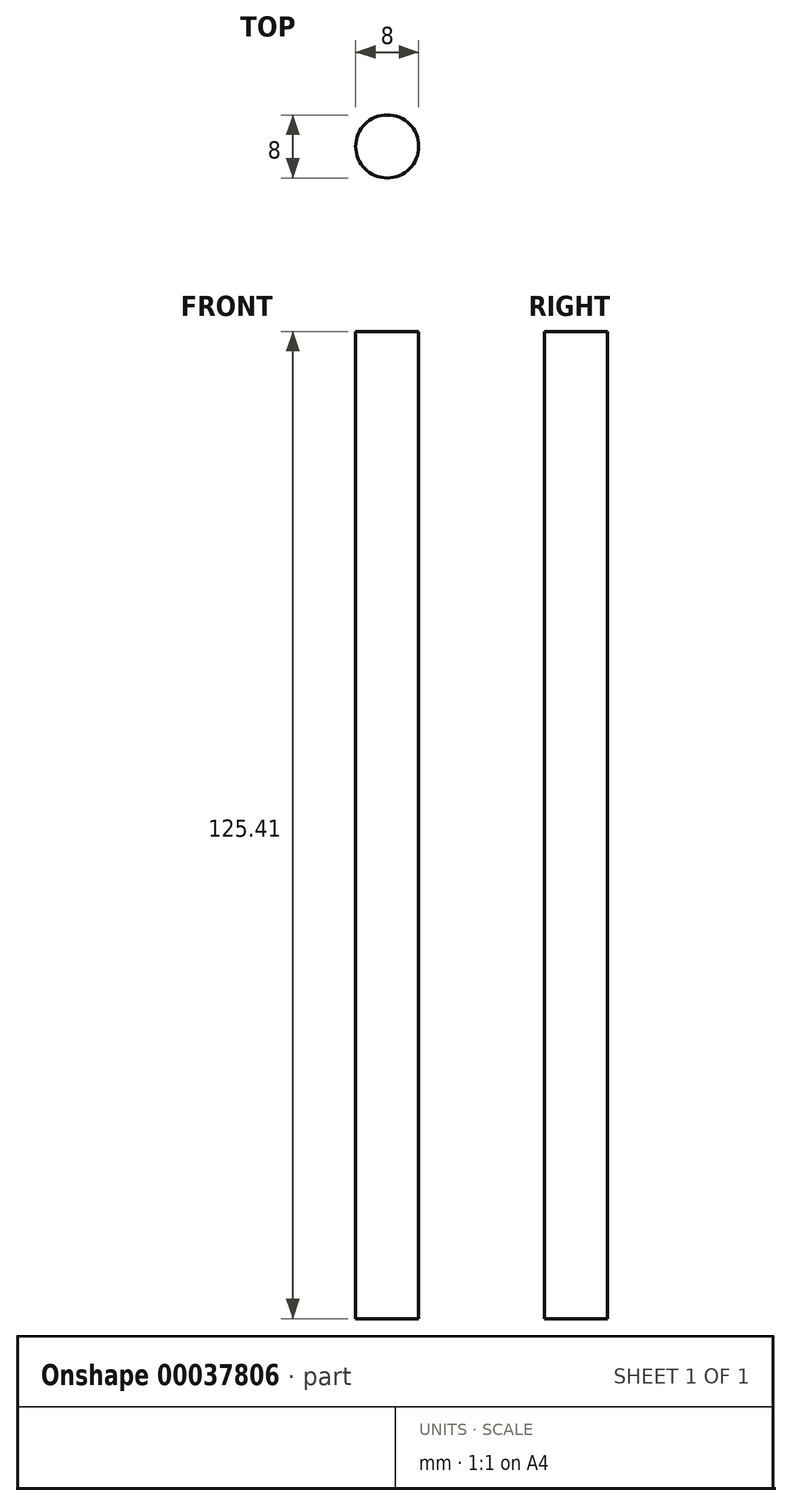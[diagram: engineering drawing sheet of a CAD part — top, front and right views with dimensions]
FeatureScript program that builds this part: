
annotation { "Feature Type Name" : "Feature", "Feature Type Description" : "" }
export const myFeature = defineFeature(function(context is Context, id is Id, definition is map)
    precondition{}
    {
        {
            var Q0;
            Q0=qCreatedBy(makeId("Top.planeOp"),FACE);
            var sketch = newSketch(context, id + "F0", { "sketchPlane" : qUnion([Q0])});
            skCircle(sketch, "E0", {"center": v(0, 0) * mm, "radius": 4 * mm});
            skSolve(sketch);
        }
        {
            var Q0;
            Q0=qSketchRegion(id+"F0",true);
            extrude(context, id + "F1", {"entities" : qUnion([Q0]), "depth" : 125.4 * mm});
        }
    });
